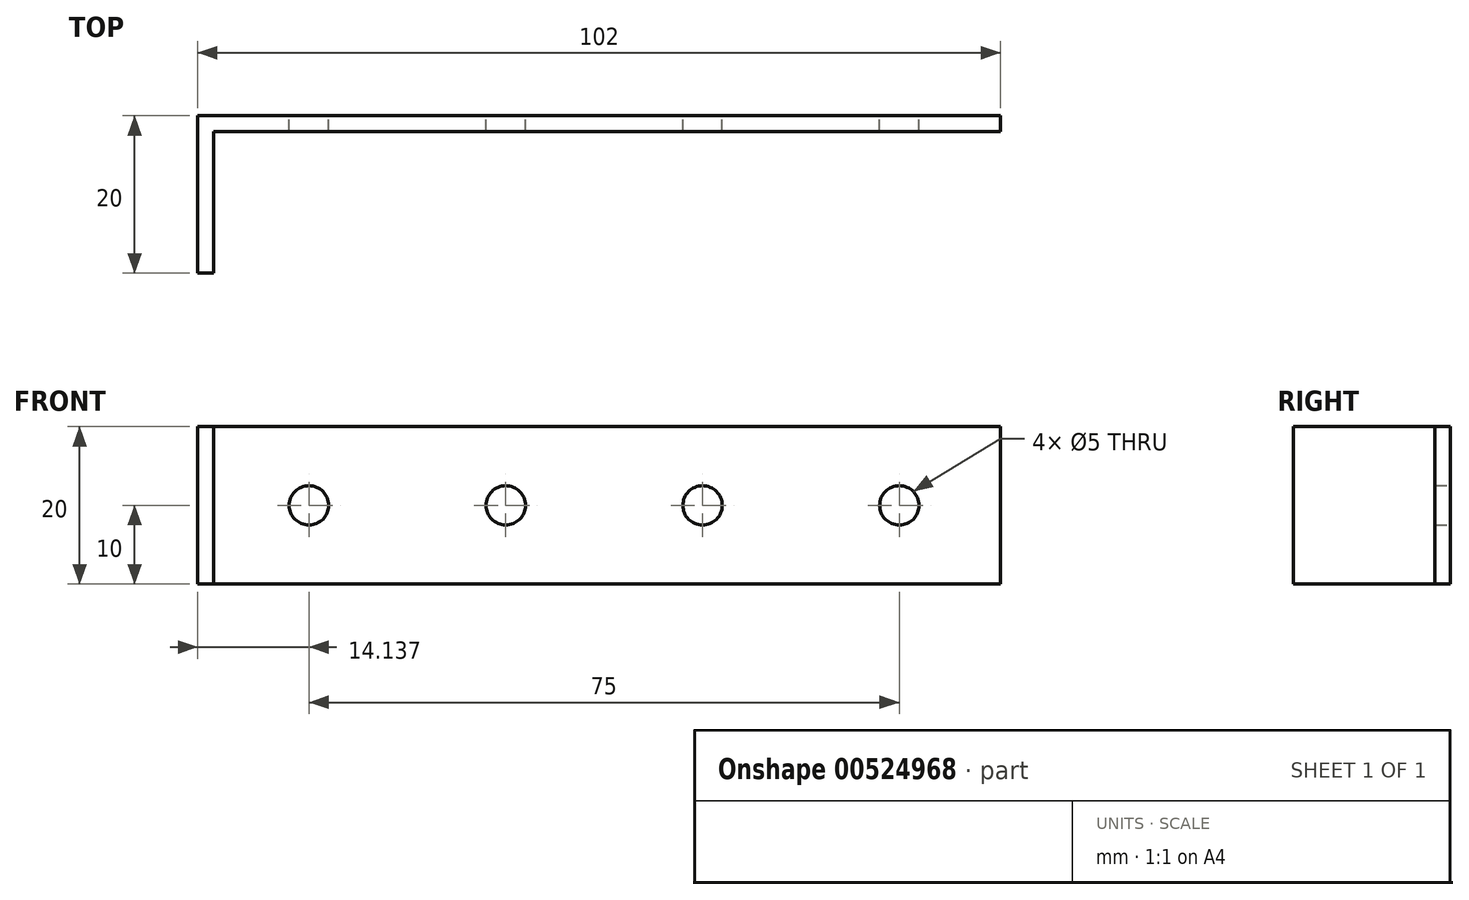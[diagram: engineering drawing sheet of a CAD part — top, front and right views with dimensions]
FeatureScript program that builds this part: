
annotation { "Feature Type Name" : "Feature", "Feature Type Description" : "" }
export const myFeature = defineFeature(function(context is Context, id is Id, definition is map)
    precondition{}
    {
        {
            var Q0;
            Q0=qCreatedBy(makeId("Front.planeOp"),FACE);
            var sketch = newSketch(context, id + "F0", { "sketchPlane" : qUnion([Q0])});
            skLineSegment(sketch, "E0.bottom", {"start": v(0, 0) * mm, "end": v(-100, 0) * mm});
            skLineSegment(sketch, "E0.top", {"start": v(0, 20) * mm, "end": v(-100, 20) * mm});
            skLineSegment(sketch, "E0.left", {"start": v(0, 0) * mm, "end": v(0, 20) * mm});
            skLineSegment(sketch, "E0.right", {"start": v(-100, 0) * mm, "end": v(-100, 20) * mm});
            skCircle(sketch, "E1", {"center": v(-87.86, 10) * mm, "radius": 2.5 * mm});
            skPoint(sketch, "E1.centerSnap0", {"position": v(-100, 10) * mm});
            skCircle(sketch, "E2.1.0.0", {"center": v(-62.86, 10) * mm, "radius": 2.5 * mm});
            skCircle(sketch, "E2.2.0.0", {"center": v(-37.86, 10) * mm, "radius": 2.5 * mm});
            skCircle(sketch, "E2.3.0.0", {"center": v(-12.86, 10) * mm, "radius": 2.5 * mm});
            skLineSegment(sketch, "E2.direction1", {"start": v(-87.86, 10) * mm, "end": v(-62.86, 10) * mm, "construction": true});
            skSolve(sketch);
        }
        {
            var Q0;
            Q0 = qSketchRegion(id + "F0", true);
            extrude(context, id + "F1", {"entities" : qUnion([Q0]), "depth" : 2 * mm, "offsetDistance" : 25 * mm});
        }
        {
            var Q0;
            Q0=makeQuery(id+"F1.opExtrude","SWEPT_FACE",FACE,{"disambiguationData":[OSD([sQuery(id+"F0.wireOp",EDGE,"E0.right")])]});
            var sketch = newSketch(context, id + "F2", { "sketchPlane" : qUnion([Q0])});
            skLineSegment(sketch, "E3.bottom", {"start": v(0, 0) * mm, "end": v(20, 0) * mm});
            skLineSegment(sketch, "E3.top", {"start": v(0, 20) * mm, "end": v(20, 20) * mm});
            skLineSegment(sketch, "E3.left", {"start": v(0, 0) * mm, "end": v(0, 20) * mm});
            skLineSegment(sketch, "E3.right", {"start": v(20, 0) * mm, "end": v(20, 20) * mm});
            skSolve(sketch);
        }
        {
            var Q0;
            Q0 = qSketchRegion(id + "F2", true);
            extrude(context, id + "F3", {"entities" : qUnion([Q0]), "operationType" : NewBodyOperationType.ADD, "depth" : 2 * mm, "offsetDistance" : 25 * mm});
        }
    });
